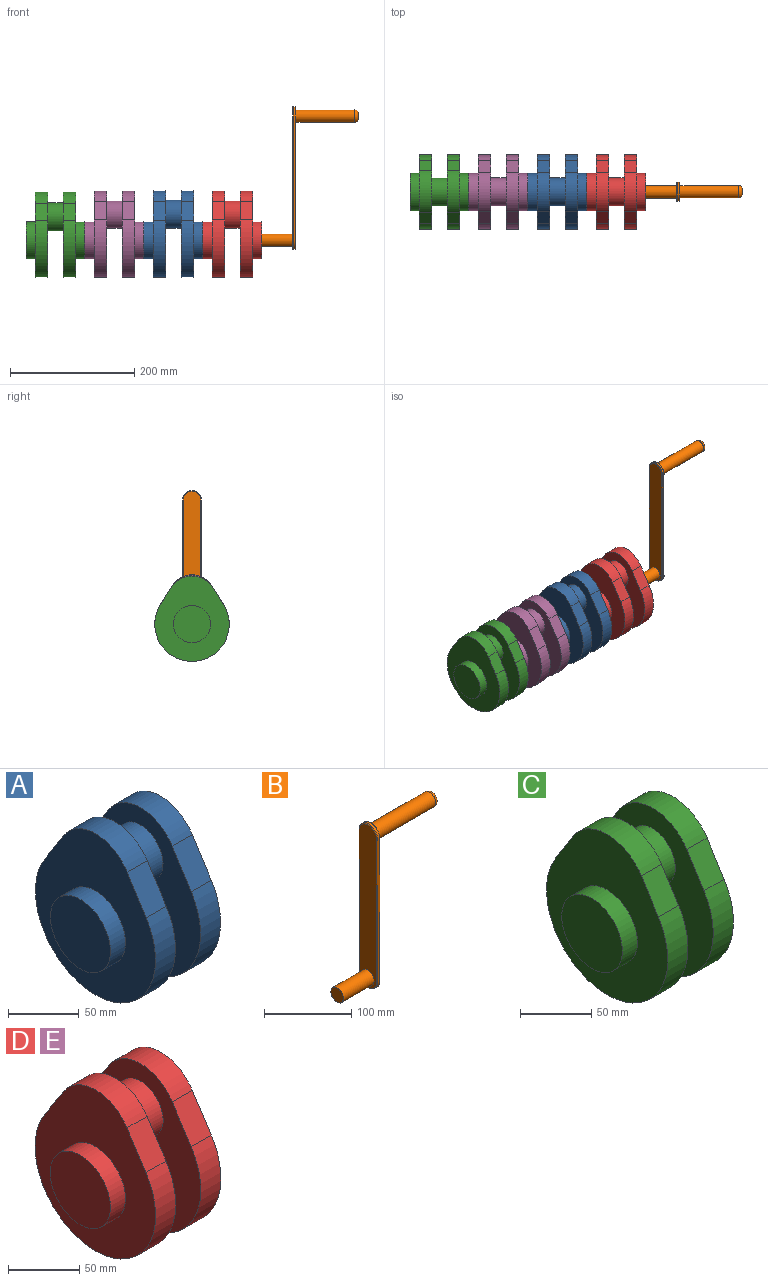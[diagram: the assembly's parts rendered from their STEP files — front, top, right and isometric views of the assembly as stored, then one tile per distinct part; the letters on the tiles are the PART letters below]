
ASSEMBLY  parts=5 mates=4
PART A: 17 faces, bbox 95x120x139.5 mm
  f0: cylinder r=30mm len=60mm, axis (-1,0,0), area 2827.4mm2, adj f1,f7
  f1: plane 60x60mm, normal (-1,0,0), area 2827.4mm2, adj f0
  f2: cylinder r=37.5mm len=63.33mm, axis (-1,0,0), area 1508.2mm2, adj f3,f5,f6,f7
  f3: plane 29.95x20mm, normal (0,-0.84,0.54), area 709.3mm2, adj f2,f4,f6,f7
  f4: cylinder r=60mm len=120mm, axis (-1,0,0), area 5126.8mm2, adj f3,f5,f6,f7
  f5: plane 29.95x20mm, normal (0,0.84,0.54), area 709.3mm2, adj f2,f4,f6,f7
  f6: plane 139.5x120mm, normal (1,0,0), area 10971.4mm2, adj f2,f3,f4,f5,f8
  f7: plane 139.5x120mm, normal (-1,0,0), area 9734.4mm2, adj f0,f2,f3,f4,f5
  f8: cylinder r=22.5mm len=45mm, axis (-1,0,0), area 3534.3mm2, adj f6,f14
  f9: cylinder r=60mm len=120mm, axis (-1,0,0), area 5126.8mm2, adj f10,f12,f13,f14
  f10: plane 29.95x20mm, normal (0,0.84,0.54), area 709.3mm2, adj f9,f11,f13,f14
  f11: cylinder r=37.5mm len=63.33mm, axis (-1,0,0), area 1508.2mm2, adj f10,f12,f13,f14
  f12: plane 29.95x20mm, normal (0,-0.84,0.54), area 709.3mm2, adj f9,f11,f13,f14
  f13: plane 139.5x120mm, normal (1,0,0), area 9734.4mm2, adj f9,f10,f11,f12,f15
  f14: plane 139.5x120mm, normal (-1,0,0), area 10971.4mm2, adj f8,f9,f10,f11,f12
  f15: cylinder r=30mm len=60mm, axis (-1,0,0), area 2827.4mm2, adj f13,f16
  f16: plane 60x60mm, normal (1,0,0), area 2827.4mm2, adj f15
PART B: 19 faces, bbox 155x32.5x232.5 mm
  f0: cylinder r=10mm len=50mm, axis (-1,0,0), area 3141.6mm2, adj f1,f7
  f1: plane 20x20mm, normal (-1,0,0), area 314.2mm2, adj f0
  f2: cylinder r=15mm len=30mm, axis (-1,0,0), area 141.4mm2, adj f3,f5,f11,f15
  f3: plane 200x3mm, normal (0,-1,0), area 600mm2, adj f2,f4,f12,f16
  f4: cylinder r=15mm len=30mm, axis (-1,0,0), area 141.4mm2, adj f3,f5,f14,f18
  f5: plane 200x3mm, normal (0,1,0), area 600mm2, adj f2,f4,f13,f17
  f6: plane 228x28mm, normal (1,0,0), area 5901.6mm2, adj f8,f15,f16,f17,f18
  f7: plane 228x28mm, normal (-1,0,0), area 5901.6mm2, adj f0,f11,f12,f13,f14
  f8: cylinder r=10mm len=95mm, axis (-1,0,0), area 5969mm2, adj f6,f10
  f9: plane 10x10mm, normal (1,0,0), area 78.5mm2, adj f10
  f10: torus R=5mm, axis (1,0,0), area 403.8mm2, adj f8,f9
  f11: torus R=14mm, axis (1,0,0), area 72.2mm2, adj f2,f7,f12,f13
  f12: cylinder r=1mm len=200mm, axis (0,0,-1), area 314.2mm2, adj f3,f7,f11,f14
  f13: cylinder r=1mm len=200mm, axis (0,0,1), area 314.2mm2, adj f5,f7,f11,f14
  f14: torus R=14mm, axis (1,0,0), area 72.2mm2, adj f4,f7,f12,f13
  f15: torus R=14mm, axis (1,0,0), area 72.2mm2, adj f2,f6,f16,f17
  f16: cylinder r=1mm len=200mm, axis (0,0,1), area 314.2mm2, adj f3,f6,f15,f18
  f17: cylinder r=1mm len=200mm, axis (0,0,-1), area 314.2mm2, adj f5,f6,f15,f18
  f18: torus R=14mm, axis (1,0,0), area 72.2mm2, adj f4,f6,f16,f17
PART C: 17 faces, bbox 95x120x137.5 mm
  f0: cylinder r=30mm len=60mm, axis (1,0,0), area 2827.4mm2, adj f1,f7
  f1: plane 60x60mm, normal (1,0,0), area 2827.4mm2, adj f0
  f2: cylinder r=40mm len=67.67mm, axis (1,0,0), area 1613.2mm2, adj f3,f5,f6,f7
  f3: plane 26.83x20mm, normal (0,0.85,0.53), area 634.4mm2, adj f2,f4,f6,f7
  f4: cylinder r=60mm len=120mm, axis (1,0,0), area 5120mm2, adj f3,f5,f6,f7
  f5: plane 26.83x20mm, normal (0,-0.85,0.53), area 634.4mm2, adj f2,f4,f6,f7
  f6: plane 137.5x120mm, normal (-1,0,0), area 10874.9mm2, adj f2,f3,f4,f5,f8
  f7: plane 137.5x120mm, normal (1,0,0), area 9637.9mm2, adj f0,f2,f3,f4,f5
  f8: cylinder r=22.5mm len=45mm, axis (1,0,0), area 3534.3mm2, adj f6,f14
  f9: plane 26.83x20mm, normal (0,-0.85,0.53), area 634.4mm2, adj f10,f12,f13,f14
  f10: cylinder r=40mm len=67.67mm, axis (1,0,0), area 1613.2mm2, adj f9,f11,f13,f14
  f11: plane 26.83x20mm, normal (0,0.85,0.53), area 634.4mm2, adj f10,f12,f13,f14
  f12: cylinder r=60mm len=120mm, axis (1,0,0), area 5120mm2, adj f9,f11,f13,f14
  f13: plane 137.5x120mm, normal (-1,0,0), area 9637.9mm2, adj f9,f10,f11,f12,f15
  f14: plane 137.5x120mm, normal (1,0,0), area 10874.9mm2, adj f8,f9,f10,f11,f12
  f15: cylinder r=30mm len=60mm, axis (1,0,0), area 2827.4mm2, adj f13,f16
  f16: plane 60x60mm, normal (-1,0,0), area 2827.4mm2, adj f15
PART D: 17 faces, bbox 95x120x138.9 mm
  f0: cylinder r=30mm len=60mm, axis (-1,0,0), area 2827.4mm2, adj f1,f7
  f1: plane 60x60mm, normal (-1,0,0), area 2827.4mm2, adj f0
  f2: cylinder r=37.5mm len=62.96mm, axis (-1,0,0), area 1494.3mm2, adj f3,f5,f6,f7
  f3: plane 29.17x20mm, normal (0,-0.84,0.54), area 695mm2, adj f2,f4,f6,f7
  f4: cylinder r=60mm len=120mm, axis (-1,0,0), area 5148.9mm2, adj f3,f5,f6,f7
  f5: plane 29.17x20mm, normal (0,0.84,0.54), area 695mm2, adj f2,f4,f6,f7
  f6: plane 138.9x120mm, normal (1,0,0), area 10922.2mm2, adj f2,f3,f4,f5,f8
  f7: plane 138.9x120mm, normal (-1,0,0), area 9685.2mm2, adj f0,f2,f3,f4,f5
  f8: cylinder r=22.5mm len=45mm, axis (-1,0,0), area 3534.3mm2, adj f6,f14
  f9: cylinder r=37.5mm len=62.96mm, axis (-1,0,0), area 1494.3mm2, adj f10,f12,f13,f14
  f10: plane 29.17x20mm, normal (0,-0.84,0.54), area 695mm2, adj f9,f11,f13,f14
  f11: cylinder r=60mm len=120mm, axis (-1,0,0), area 5148.9mm2, adj f10,f12,f13,f14
  f12: plane 29.17x20mm, normal (0,0.84,0.54), area 695mm2, adj f9,f11,f13,f14
  f13: plane 138.9x120mm, normal (1,0,0), area 9685.2mm2, adj f9,f10,f11,f12,f15
  f14: plane 138.9x120mm, normal (-1,0,0), area 10922.2mm2, adj f8,f9,f10,f11,f12
  f15: cylinder r=30mm len=60mm, axis (-1,0,0), area 2827.4mm2, adj f13,f16
  f16: plane 60x60mm, normal (1,0,0), area 2827.4mm2, adj f15
PART E: same geometry as D
PLACE A at identity fixed
PLACE B t=(190,0,0)mm
PLACE C t=(-95,0,0)mm
PLACE D t=(95,0,0)mm
PLACE E t=(-95,0,0)mm
MATE fastened E.f15 <-> A.f0  axis (1,0,0) through (0,0,0)mm
MATE fastened D.f0 <-> A.f15  axis (-1,0,0) through (95,0,0)mm
MATE fastened B.f0 <-> D.f15  axis (-1,0,0) through (190,0,0)mm
MATE fastened C.f0 <-> E.f0  axis (1,0,0) through (-95,0,0)mm
